FCSTD DOCUMENT  (FreeCAD 0.19R0.19.2)
Label: 013
License: All rights reserved
LicenseURL: http://en.wikipedia.org/wiki/All_rights_reserved
objects: Sketcher::SketchObject×1
note: 1 computed .brp shape members not serialized (recipe doc carries the construction recipe); baked Part::Feature solids carry a one-line shape summary decoded from their .brp

FEATURE [Sketcher::SketchObject] Sketch
  FullyConstrained = true
  sketch-geometry (64):
    g0: ArcOfCircle CenterX=-3.45031e-07 CenterY=0 CenterZ=0 NormalX=0 NormalY=0 NormalZ=1 AngleXU=0 Radius=10.2 StartAngle=5.4126 EndAngle=7.15377
    g1: ArcOfCircle CenterX=-3.45031e-07 CenterY=0 CenterZ=0 NormalX=0 NormalY=0 NormalZ=1 AngleXU=0 Radius=10.2 StartAngle=2.27101 EndAngle=4.01218
    g2: LineSegment StartX=-6.57267 StartY=7.8 StartZ=0 EndX=6.57267 EndY=7.8 EndZ=0
    g3: LineSegment StartX=-6.57267 StartY=-7.8 StartZ=0 EndX=6.57267 EndY=-7.8 EndZ=0
    g4: ArcOfCircle CenterX=-3.45031e-07 CenterY=0 CenterZ=0 NormalX=0 NormalY=0 NormalZ=1 AngleXU=0 Radius=11.6 StartAngle=2.27101 EndAngle=2.66709
    g5: ArcOfCircle CenterX=-3.45031e-07 CenterY=0 CenterZ=0 NormalX=0 NormalY=0 NormalZ=1 AngleXU=0 Radius=11.6 StartAngle=5.4126 EndAngle=5.80868
    g6: LineSegment StartX=-7.4748 StartY=8.87059 StartZ=0 EndX=7.4748 EndY=8.87059 EndZ=0
    g7: LineSegment StartX=-7.4748 StartY=-8.87059 StartZ=0 EndX=7.4748 EndY=-8.87059 EndZ=0
    g8: LineSegment StartX=-30.2 StartY=2.5 StartZ=0 EndX=-30.2 EndY=3.5 EndZ=0
    g9: LineSegment StartX=30.2 StartY=2.5 StartZ=0 EndX=30.2 EndY=3.5 EndZ=0
    g10: LineSegment StartX=-30.2 StartY=-2.5 StartZ=0 EndX=-30.2 EndY=-3.5 EndZ=0
    g11: LineSegment StartX=30.2 StartY=-2.5 StartZ=0 EndX=30.2 EndY=-3.5 EndZ=0
    g12: LineSegment StartX=-30.2 StartY=3.5 StartZ=0 EndX=-28.8 EndY=3.5 EndZ=0
    g13: LineSegment StartX=-30.2 StartY=-3.5 StartZ=0 EndX=-28.8 EndY=-3.5 EndZ=0
    g14: LineSegment StartX=30.2 StartY=3.5 StartZ=0 EndX=28.8 EndY=3.5 EndZ=0
    g15: LineSegment StartX=30.2 StartY=-3.5 StartZ=0 EndX=28.8 EndY=-3.5 EndZ=0
    g16: ArcOfCircle CenterX=-3.45031e-07 CenterY=0 CenterZ=0 NormalX=0 NormalY=0 NormalZ=1 AngleXU=0 Radius=11.6 StartAngle=3.6161 EndAngle=4.01218
    g17: ArcOfCircle CenterX=-3.45031e-07 CenterY=0 CenterZ=0 NormalX=0 NormalY=0 NormalZ=1 AngleXU=0 Radius=11.6 StartAngle=0.474503 EndAngle=0.870585
    g18: Circle CenterX=-28.8 CenterY=3.5 CenterZ=0 NormalX=0 NormalY=0 NormalZ=1 AngleXU=0 Radius=1
    g19: Circle CenterX=-10.9247 CenterY=3.9 CenterZ=0 NormalX=0 NormalY=0 NormalZ=1 AngleXU=0 Radius=1
    g20: Circle CenterX=-10.3184 CenterY=5.3 CenterZ=0 NormalX=0 NormalY=0 NormalZ=1 AngleXU=0 Radius=1
    g21: BSplineCurve PolesCount=3 KnotsCount=2 Degree=2 IsPeriodic=0
    g22: GeomPoint X=-28.8 Y=3.5 Z=0
    g23: GeomPoint X=-10.3184 Y=5.3 Z=0
    g24: Circle CenterX=28.8 CenterY=3.5 CenterZ=0 NormalX=0 NormalY=0 NormalZ=1 AngleXU=0 Radius=1
    g25: Circle CenterX=10.9247 CenterY=3.9 CenterZ=0 NormalX=0 NormalY=0 NormalZ=1 AngleXU=0 Radius=1
    g26: Circle CenterX=10.3184 CenterY=5.3 CenterZ=0 NormalX=0 NormalY=0 NormalZ=1 AngleXU=0 Radius=1
    g27: BSplineCurve PolesCount=3 KnotsCount=2 Degree=2 IsPeriodic=0
    g28: GeomPoint X=28.8 Y=3.5 Z=0
    g29: GeomPoint X=10.3184 Y=5.3 Z=0
    g30: Circle CenterX=-28.8 CenterY=-3.5 CenterZ=0 NormalX=0 NormalY=0 NormalZ=1 AngleXU=0 Radius=1
    g31: Circle CenterX=-10.9247 CenterY=-3.9 CenterZ=0 NormalX=0 NormalY=0 NormalZ=1 AngleXU=0 Radius=1
    g32: Circle CenterX=-10.3184 CenterY=-5.3 CenterZ=0 NormalX=0 NormalY=0 NormalZ=1 AngleXU=0 Radius=1
    g33: BSplineCurve PolesCount=3 KnotsCount=2 Degree=2 IsPeriodic=0
    g34: GeomPoint X=-28.8 Y=-3.5 Z=0
    g35: GeomPoint X=-10.3184 Y=-5.3 Z=0
    g36: Circle CenterX=28.8 CenterY=-3.5 CenterZ=0 NormalX=0 NormalY=0 NormalZ=1 AngleXU=0 Radius=1
    g37: Circle CenterX=10.9247 CenterY=-3.9 CenterZ=0 NormalX=0 NormalY=0 NormalZ=1 AngleXU=0 Radius=1
    g38: Circle CenterX=10.3184 CenterY=-5.3 CenterZ=0 NormalX=0 NormalY=0 NormalZ=1 AngleXU=0 Radius=1
    g39: BSplineCurve PolesCount=3 KnotsCount=2 Degree=2 IsPeriodic=0
    g40: GeomPoint X=28.8 Y=-3.5 Z=0
    g41: GeomPoint X=10.3184 Y=-5.3 Z=0
    g42-g46: Circle x5 (B-spline internal-alignment scaffolding for g47; pole/knot coordinates omitted)
    g47: BSplineCurve PolesCount=5 KnotsCount=3 Degree=3 IsPeriodic=0
    g48: GeomPoint X=12.7274 Y=2.5 Z=0
    g49: GeomPoint X=11.4637 Y=2.49999e-07 Z=0
    g50: GeomPoint X=12.7274 Y=-2.5 Z=0
    g51-g55: Circle x5 (B-spline internal-alignment scaffolding for g56; pole/knot coordinates omitted)
    g56: BSplineCurve PolesCount=5 KnotsCount=3 Degree=3 IsPeriodic=0
    g57: GeomPoint X=-12.7274 Y=2.5 Z=0
    g58: GeomPoint X=-11.4637 Y=2.50004e-07 Z=0
    g59: GeomPoint X=-12.7274 Y=-2.5 Z=0
    g60: LineSegment StartX=-30.2 StartY=-2.5 StartZ=0 EndX=-12.7274 EndY=-2.5 EndZ=0
    g61: LineSegment StartX=-30.2 StartY=2.5 StartZ=0 EndX=-12.7274 EndY=2.5 EndZ=0
    g62: LineSegment StartX=30.2 StartY=2.5 StartZ=0 EndX=12.7274 EndY=2.5 EndZ=0
    g63: LineSegment StartX=30.2 StartY=-2.5 StartZ=0 EndX=12.7274 EndY=-2.5 EndZ=0
  constraints (119):
    c: Block(g0)
    c: Equal(g0,g1)
    c: Coincident(g0,g1)
    c: Coincident(g2,g1)
    c: Coincident(g2,g0)
    c: Horizontal(g2)
    c: Coincident(g3,g1)
    c: Coincident(g3,g0)
    c: Horizontal(g3)
    c: Block(g2)
    c: Block(g3)
    c: Coincident(g4,g0)
    c: Coincident(g5,g0)
    c: Block(g5)
    c: Block(g4)
    c: Coincident(g6,g4)
    c: Coincident(g6,g17)
    c: Horizontal(g6)
    c: Coincident(g7,g16)
    c: Coincident(g7,g5)
    c: Horizontal(g7)
    c: Vertical(g8)
    c: Distance(g8) = 1
    c: Vertical(g9)
    c: Distance(g9) = 1
    c: Distance(g10) = 1
    c: Vertical(g11)
    c: Distance(g11) = 1
    c: Coincident(g12,g8)
    c: Horizontal(g12)
    c: Distance(g12) = 1.4
    c: Horizontal(g13)
    c: Equal(g12,g13) = 1.4
    c: Coincident(g13,g10)
    c: Coincident(g14,g9)
    c: Horizontal(g14)
    c: Distance(g14) = 1.4
    c: Horizontal(g15)
    c: Equal(g14,g15) = 1.4
    c: Coincident(g15,g11)
    c: Equal(g4,g16)
    c: Coincident(g4,g16)
    c: Equal(g5,g17)
    c: Coincident(g5,g17)
    c: Block(g16)
    c: Block(g17)
    c: Coincident(g21,g12)
    c: Weight(g18) = 1
    c: Equal(g18,g19)
    c: Equal(g18,g20)
    c: Coincident(g21,g4)
    c: InternalAlignment(g18,g21)
    c: InternalAlignment(g19,g21)
    c: InternalAlignment(g20,g21)
    c: InternalAlignment(g22,g21)
    c: InternalAlignment(g23,g21)
    c: Coincident(g27,g14)
    c: Weight(g24) = 1
    c: Equal(g24,g25)
    c: Equal(g24,g26)
    c: Coincident(g27,g17)
    c: InternalAlignment(g24,g27)
    c: InternalAlignment(g25,g27)
    c: InternalAlignment(g26,g27)
    c: InternalAlignment(g28,g27)
    c: InternalAlignment(g29,g27)
    c: Coincident(g33,g13)
    c: Weight(g30) = 1
    c: Equal(g30,g31)
    c: Equal(g30,g32)
    c: Coincident(g33,g16)
    c: InternalAlignment(g30,g33)
    c: InternalAlignment(g31,g33)
    c: InternalAlignment(g32,g33)
    c: InternalAlignment(g34,g33)
    c: InternalAlignment(g35,g33)
    c: Coincident(g39,g15)
    c: Weight(g36) = 1
    c: Equal(g36,g37)
    c: Equal(g36,g38)
    c: Coincident(g39,g5)
    c: InternalAlignment(g36,g39)
    c: InternalAlignment(g37,g39)
    c: InternalAlignment(g38,g39)
    c: InternalAlignment(g40,g39)
    c: InternalAlignment(g41,g39)
    c: Block(g27)
    c: Block(g21)
    c: Block(g39)
    c: Block(g33)
    c: Weight(g42) = 1
    c: Equal(g42, g43-g46) x4
    c: InternalAlignment(g42-g46 -> g47) x5
    c: InternalAlignment(g48,g47)
    c: InternalAlignment(g49,g47)
    c: InternalAlignment(g50,g47)
    c: Weight(g51) = 1
    c: Equal(g51,g52)
    c: Equal(g51,g53)
    c: Equal(g51,g54)
    c: InternalAlignment(g51-g55 -> g56) x5
    c: InternalAlignment(g57,g56)
    c: InternalAlignment(g58,g56)
    c: InternalAlignment(g59,g56)
    c: Block(g56)
    c: Block(g47)
    c: Block(g10)
    c: Coincident(g60,g10)
    c: Coincident(g60,g56)
    c: Tangent(g60,g30)
    c: Coincident(g61,g8)
    c: Coincident(g61,g56)
    c: Tangent(g61,g18)
    c: Coincident(g62,g9)
    c: Coincident(g62,g47)
    c: Tangent(g62,g24)
    c: Coincident(g63,g11)
    c: Coincident(g63,g47)
    c: Tangent(g63,g36)
